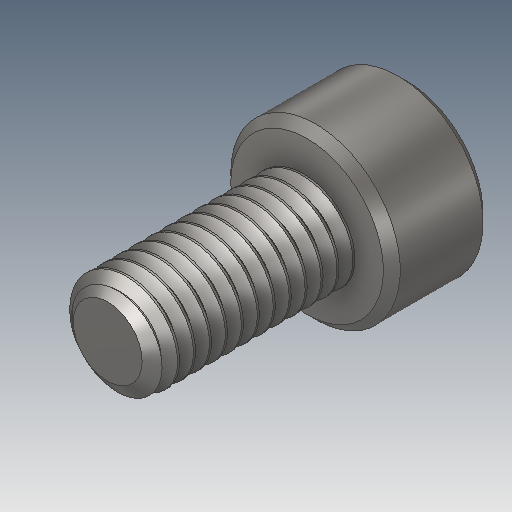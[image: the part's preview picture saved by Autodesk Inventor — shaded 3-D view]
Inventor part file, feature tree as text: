
AUTODESK INVENTOR PART (.ipt)
format: ipt  version: 2018 (Build 220112000, 112)  size: 538,624 bytes
history: native  units: in
note: dims shown in document units (in); Inventor stores cm internally (conversion verified against a paired STEP export)
features: chamfer x1
ambient origin geometry x8: Origin, YZ Plane, XZ Plane, XY Plane, X Axis, Y Axis, Z Axis, Center Point
bodies: Solid1 (feature_tree)
feature tree (1):
  chamfer  "Chamfer1"  [1 undecoded]
note: 1 required parameter value undecoded (feature->parameter linkage not recoverable at this tier; creation-order binding heuristic only, values carry confidence <= 0.55)
